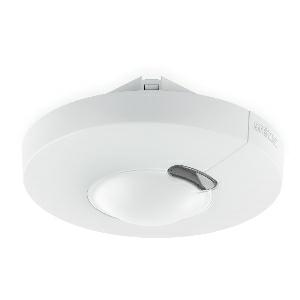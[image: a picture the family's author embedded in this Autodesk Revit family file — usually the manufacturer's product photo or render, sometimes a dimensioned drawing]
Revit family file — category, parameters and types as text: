
# Revit family: hf_3360_033712
name_source: partatom
category: Elektroinstallationen
revit_build: Autodesk Revit 2016 (Build: 20190508_0715(x64)
units: mm (PartAtom-declared; Revit-internal decimal feet)

## family parameters
Basisbauteil = Fläche
Beim Laden mit Abzugskörper schneiden = Nein
Bemaßung runder Anschluss = Durchmesser verwenden
Beschriftungsausrichtung beibehalten = Nein
Gemeinsam genutzt = Nein
Raumberechnungspunkt = Nein
Teiletyp = Normal

## types (1)
- HF 3360
    Apparent Load = 0 VA
    Beschreibung = Type: Motion detectors; Dimensions (Ø x H): 124 x 64 mm; Mains power supply: 220 – 240 V / 50 – 60 Hz; Sensor Technology: High frequency; Application, place: Indoors; Application, room: function room / ancillary room, stairwell, WC / washroom, multi-storey / underground car park, Indoors; Installation site: wall, ceiling, corner; Installation: Concealed wiring; HF-system: 5,8 GHz; Electronic scalability: Yes; Mechanical scalability: No; Mounting height: 2,00 – 4,00 m; Optimum mounting height: 2,8 m; Detection: also through glass, wood and stud walls; Detection angle: 360 °; Angle of aperture: 140 °; Sneak-by guard: Yes; Reach, radial: Ø 8 m (50 m²); Reach, tangential: Ø 8 m (50 m²); Twilight setting TEACH: Yes; Twilight setting: 2 – 1000 lx; Time setting: 5 sec – 15 min; Constant-lighting control: No; Basic light level function: No; Functions: Normal / test mode, Manual ON / ON-OFF; Settings via: Remote control, Potentiometers, Smart Remote; With remote control: No; Interconnection: Yes; IP-rating: IP20; Material: Plastic; Ambient temperature: -20 – 50 °C; Colour: white; Colour, RAL: 9003; Manufacturer's Warranty: 5 years; Version: PF - concealed, rd.; PU1, EAN: 4007841033712
    Height = 0 mm  [stored 0 ft]
    Hersteller = Steinel
    Length = 124 mm  [stored 0.406824 ft]
    ModVariant = Nein
    Modell = 033712
    Mounting Type = Recessed
    Number of Poles = 1
    OnlyDefault = Ja
    Power Factor = 1
    Product Name = HF 3360
    Product group = Sensor-switched indoor light
    ProductGroupID = 30
    Protection Class = Protection class
    Protection Degree = IP 20
    RlxData = <blob elided: 36297 chars, md5=35994872>
    SensorDataFile = {"IESDataFiles":[]}
    Typenbild = produkt1_033712.jpg
    Typenkommentare = Product without accessories
    URL = http://relux.com
    VarID = ---
    Voltage = 0 V
    Vorgabe-Ansicht = 1800 mm
    Weight = 0.00 kg
    Width = 0 mm  [stored 0 ft]

note: [stored X ft] marks values corroborated as IEEE doubles in the binary element streams (Revit-internal decimal feet)

## geometry (parser evidence)
native form markers: Sweep x9
no freeform markers — native parametric forms only
